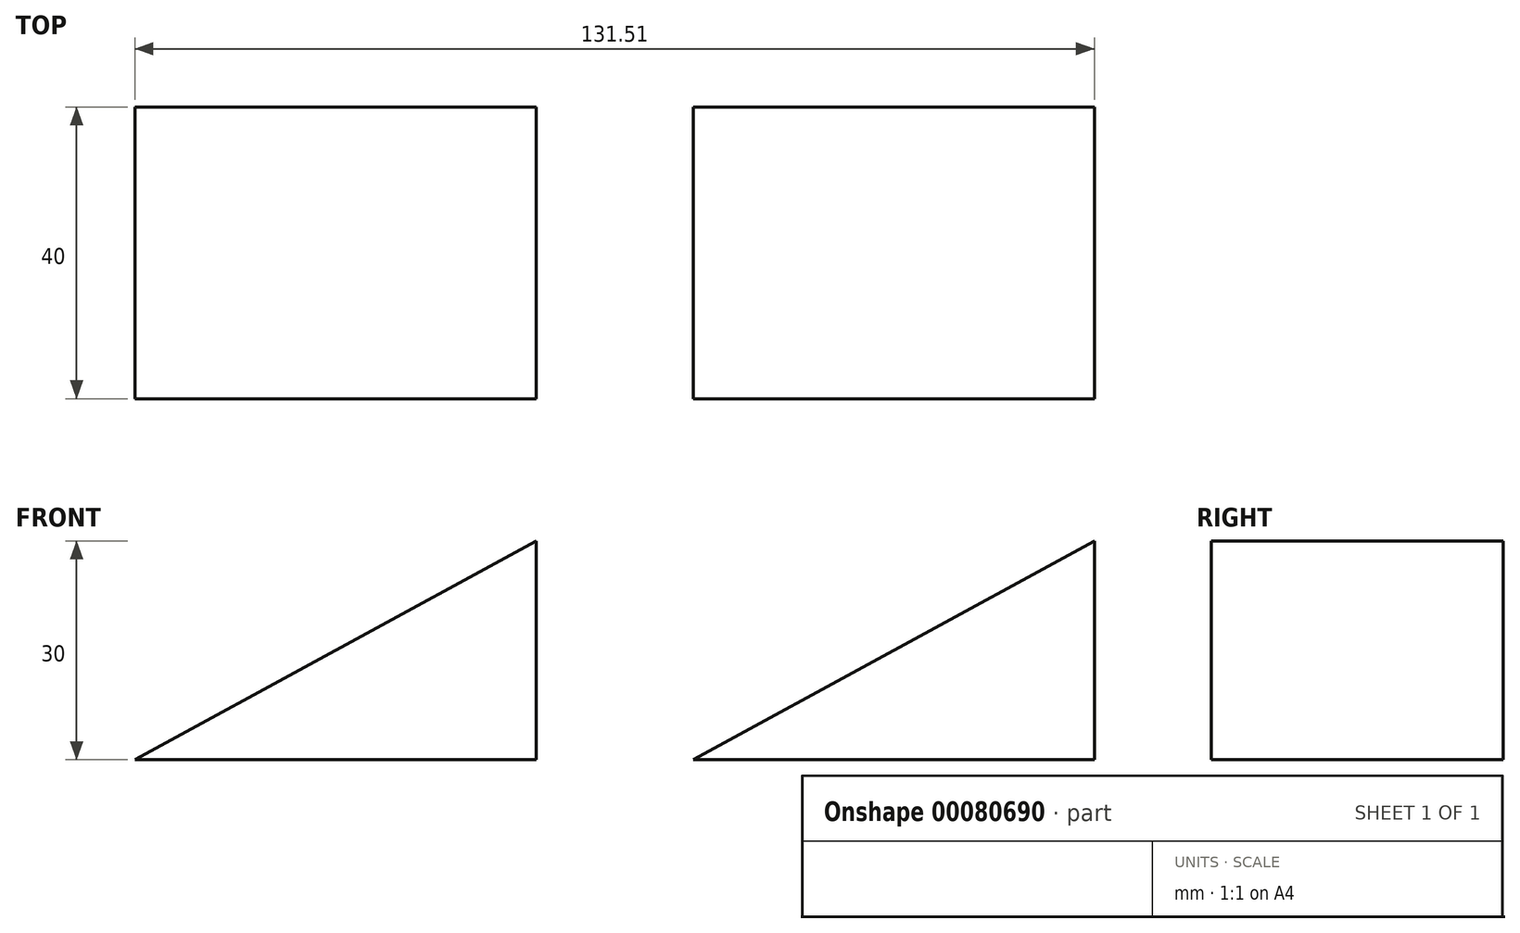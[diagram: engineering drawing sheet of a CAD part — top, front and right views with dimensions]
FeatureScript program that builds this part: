
annotation { "Feature Type Name" : "Feature", "Feature Type Description" : "" }
export const myFeature = defineFeature(function(context is Context, id is Id, definition is map)
    precondition{}
    {
        {
            var Q0;
            Q0=qCreatedBy(makeId("Front.planeOp"),FACE);
            var sketch = newSketch(context, id + "F0", { "sketchPlane" : qUnion([Q0])});
            skLineSegment(sketch, "E0", {"start": v(56.63, 18.98) * mm, "end": v(56.63, -11.02) * mm});
            skLineSegment(sketch, "E1", {"start": v(56.63, -11.02) * mm, "end": v(1.63, -11.02) * mm});
            skLineSegment(sketch, "E2", {"start": v(1.63, -11.02) * mm, "end": v(56.63, 18.98) * mm});
            skLineSegment(sketch, "E3", {"start": v(78.14, -11.02) * mm, "end": v(133.14, -11.02) * mm});
            skLineSegment(sketch, "E4", {"start": v(133.14, -11.02) * mm, "end": v(133.14, 18.98) * mm});
            skLineSegment(sketch, "E5", {"start": v(133.14, 18.98) * mm, "end": v(78.14, -11.02) * mm});
            skSolve(sketch);
        }
        {
            var Q0;
            Q0=makeQuery(id+"F0.imprint","IMPRINT",FACE,{"disambiguationData":[TD([[makeQuery(id+"F0.imprint","IMPRINT",EDGE,{"derivedFrom":sQuery(id+"F0.wireOp",EDGE,"xOkpwOxA-eSaq-Io9L-jU8P-NK8npNRvJ1KN")}),-1.0]])]});
            var Q1;
            Q1=makeQuery(id+"F0.imprint","IMPRINT",FACE,{"disambiguationData":[TD([[makeQuery(id+"F0.imprint","IMPRINT",EDGE,{"derivedFrom":sQuery(id+"F0.wireOp",EDGE,"E0")}),-1.0]])]});
            var Q2;
            Q2=makeQuery(id+"F0.imprint","IMPRINT",FACE,{"disambiguationData":[TD([[makeQuery(id+"F0.imprint","IMPRINT",EDGE,{"derivedFrom":sQuery(id+"F0.wireOp",EDGE,"E3")}),1.0]])]});
            extrude(context, id + "F1", {"entities" : qUnion([Q0, Q1, Q2]), "depth" : 40 * mm});
        }
    });
